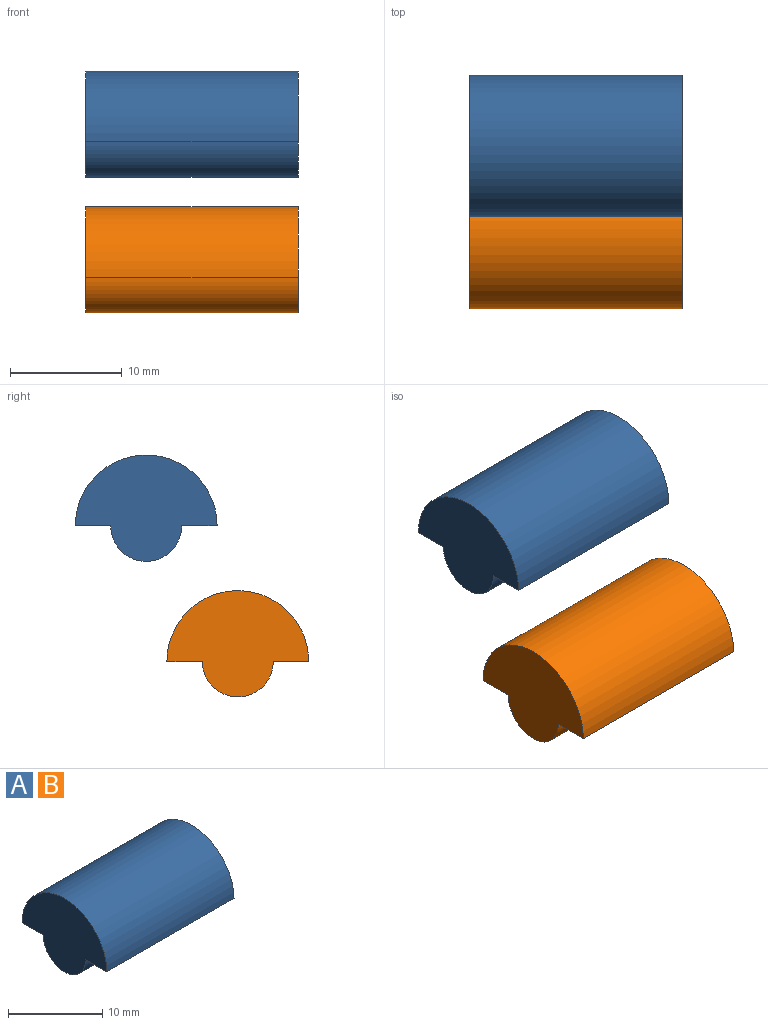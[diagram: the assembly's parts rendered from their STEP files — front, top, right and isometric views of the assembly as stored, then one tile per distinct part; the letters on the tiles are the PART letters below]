
ASSEMBLY  parts=2 mates=1
PART A: 6 faces, bbox 19.1x12.7x9.5 mm
  f0: plane 19.05x3.18mm, normal (0,0,-1), area 60.5mm2, adj f1,f3,f4,f5
  f1: cylinder r=3.17mm len=19.05mm, axis (-1,0,0), area 190mm2, adj f0,f2,f4,f5
  f2: plane 19.05x3.18mm, normal (0,0,-1), area 60.5mm2, adj f1,f3,f4,f5
  f3: cylinder r=6.35mm len=19.05mm, axis (-1,0,0), area 380mm2, adj f0,f2,f4,f5
  f4: plane 12.7x9.53mm, normal (1,0,0), area 79.2mm2, adj f0,f1,f2,f3
  f5: plane 12.7x9.53mm, normal (-1,0,0), area 79.2mm2, adj f0,f1,f2,f3
PART B: same geometry as A
PLACE A rot(axis=(0,-1,0),0deg) t=(8.83,28.65,-14.98)mm
PLACE B rot(axis=(0,-1,0),0deg) t=(8.83,20.45,-27.13)mm
MATE planar B.f5 <-> A.f5  axis (-1,0,0) through (8.83,20.45,-25.24)mm
